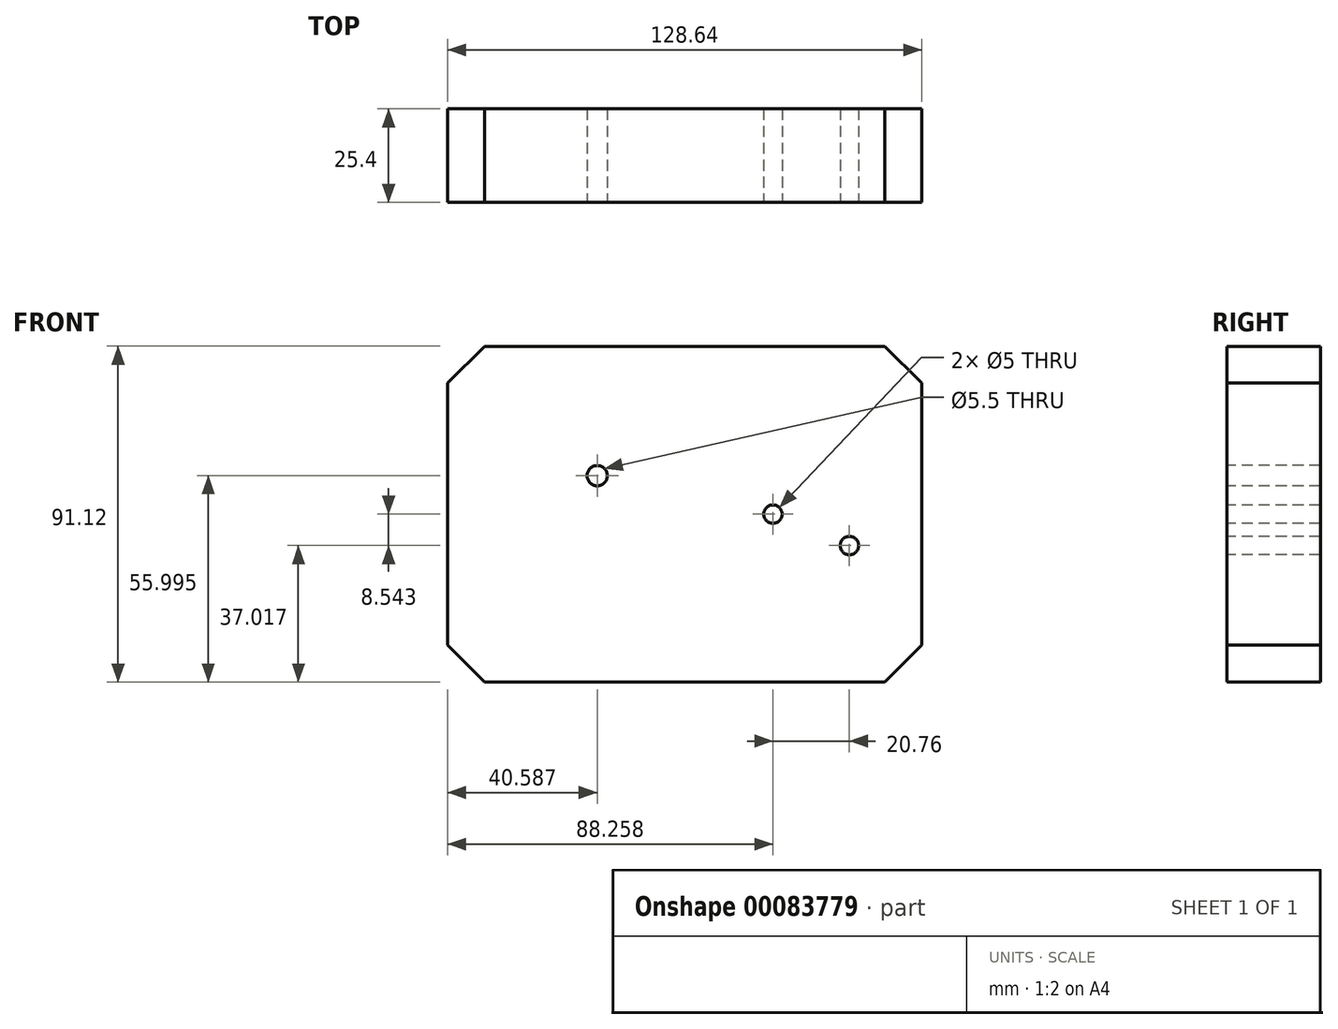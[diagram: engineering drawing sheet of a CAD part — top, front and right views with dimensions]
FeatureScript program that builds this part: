
annotation { "Feature Type Name" : "Feature", "Feature Type Description" : "" }
export const myFeature = defineFeature(function(context is Context, id is Id, definition is map)
    precondition{}
    {
        {
            var Q0;
            Q0=qCreatedBy(makeId("Front.planeOp"),FACE);
            var sketch = newSketch(context, id + "F0", { "sketchPlane" : qUnion([Q0])});
            skLineSegment(sketch, "E0.bottom", {"start": v(64.32, -45.56) * mm, "end": v(-64.32, -45.56) * mm});
            skLineSegment(sketch, "E0.top", {"start": v(64.32, 45.56) * mm, "end": v(-64.32, 45.56) * mm});
            skLineSegment(sketch, "E0.left", {"start": v(64.32, -45.56) * mm, "end": v(64.32, 45.56) * mm});
            skLineSegment(sketch, "E0.right", {"start": v(-64.32, -45.56) * mm, "end": v(-64.32, 45.56) * mm});
            skPoint(sketch, "E0.middle", {"position": v(0, 0) * mm});
            skSolve(sketch);
        }
        {
            var Q0;
            Q0 = qSketchRegion(id + "F0", true);
            extrude(context, id + "F1", {"entities" : qUnion([Q0]), "depth" : 25.4 * mm});
        }
        {
            var Q0;
            Q0=makeQuery(id+"F1.opExtrude","CAP_FACE",FACE,{"disambiguationData":[OSD([sQuery(id+"F0.wireOp",EDGE,"E0.bottom"),sQuery(id+"F0.wireOp",EDGE,"E0.top"),sQuery(id+"F0.wireOp",EDGE,"E0.left"),sQuery(id+"F0.wireOp",EDGE,"E0.right")])],"isStart":false});
            var sketch = newSketch(context, id + "F2", { "sketchPlane" : qUnion([Q0])});
            skPoint(sketch, "E1", {"position": v(23.94, 0) * mm});
            skPoint(sketch, "E2", {"position": v(44.7, -8.54) * mm});
            skSolve(sketch);
        }
        {
            var Q0;
            Q0=sQuery(id+"F2.wireOp",VERTEX,"E1");
            var Q1;
            Q1=sQuery(id+"F2.wireOp",VERTEX,"E2");
            var Q2;
            Q2=makeQuery(id+"F1.opExtrude","SWEPT_BODY",BODY,{"disambiguationData":[OSD([sQuery(id+"F0.wireOp",EDGE,"E0.bottom"),sQuery(id+"F0.wireOp",EDGE,"E0.top"),sQuery(id+"F0.wireOp",EDGE,"E0.left"),sQuery(id+"F0.wireOp",EDGE,"E0.right")])]});
            hole(context, id + "F6", {"style" : HoleStyle.SIMPLE, "endStyle" : HoleEndStyle.THROUGH, "holeDiameter" : 5 * mm, "locations" : qUnion([Q0, Q1]), "scope" : qUnion([Q2]), "isTappedThrough" : true});
        }
        {
            var Q0;
            Q0=makeQuery(id+"F1.opExtrude","SWEPT_EDGE",EDGE,{"disambiguationData":[OSD([sQuery(id+"F0.wireOp",EDGE,"E0.top"),sQuery(id+"F0.wireOp",EDGE,"E0.left")])]});
            var Q1;
            Q1=makeQuery(id+"F1.opExtrude","SWEPT_EDGE",EDGE,{"disambiguationData":[OSD([sQuery(id+"F0.wireOp",EDGE,"E0.bottom"),sQuery(id+"F0.wireOp",EDGE,"E0.left")])]});
            var Q2;
            Q2=makeQuery(id+"F1.opExtrude","SWEPT_EDGE",EDGE,{"disambiguationData":[OSD([sQuery(id+"F0.wireOp",EDGE,"E0.bottom"),sQuery(id+"F0.wireOp",EDGE,"E0.right")])]});
            var Q3;
            Q3=makeQuery(id+"F1.opExtrude","SWEPT_EDGE",EDGE,{"disambiguationData":[OSD([sQuery(id+"F0.wireOp",EDGE,"E0.top"),sQuery(id+"F0.wireOp",EDGE,"E0.right")])]});
            chamfer(context, id + "F3", {"entities" : qUnion([Q0, Q1, Q2, Q3]), "width" : 10 * mm, "tangentPropagation" : true});
        }
        {
            var Q0;
            Q0=makeQuery(id+"F1.opExtrude","CAP_FACE",FACE,{"disambiguationData":[OSD([sQuery(id+"F0.wireOp",EDGE,"E0.bottom"),sQuery(id+"F0.wireOp",EDGE,"E0.top"),sQuery(id+"F0.wireOp",EDGE,"E0.left"),sQuery(id+"F0.wireOp",EDGE,"E0.right")])],"isStart":false});
            var sketch = newSketch(context, id + "F4", { "sketchPlane" : qUnion([Q0])});
            skPoint(sketch, "E3", {"position": v(-23.73, 10.44) * mm});
            skSolve(sketch);
        }
        {
            var Q0;
            Q0=sQuery(id+"F4.wireOp",VERTEX,"E3");
            var Q1;
            Q1=makeQuery(id+"F1.opExtrude","SWEPT_BODY",BODY,{"disambiguationData":[OSD([sQuery(id+"F0.wireOp",EDGE,"E0.bottom"),sQuery(id+"F0.wireOp",EDGE,"E0.top"),sQuery(id+"F0.wireOp",EDGE,"E0.left"),sQuery(id+"F0.wireOp",EDGE,"E0.right")])]});
            hole(context, id + "F5", {"style" : HoleStyle.SIMPLE, "endStyle" : HoleEndStyle.THROUGH, "standardTappedOrClearance" : lookupTablePath({ "standard" : "ISO", "fit" : "Normal", "size" : "M5", "type" : "Clearance" }), "standardBlindInLast" : lookupTablePath({ "fit" : "Standard", "standard" : "ISO", "size" : "M5", "type" : "Clearance" }), "holeDiameter" : 5.5 * mm, "locations" : qUnion([Q0]), "scope" : qUnion([Q1]), "isTappedThrough" : true});
        }
    });
